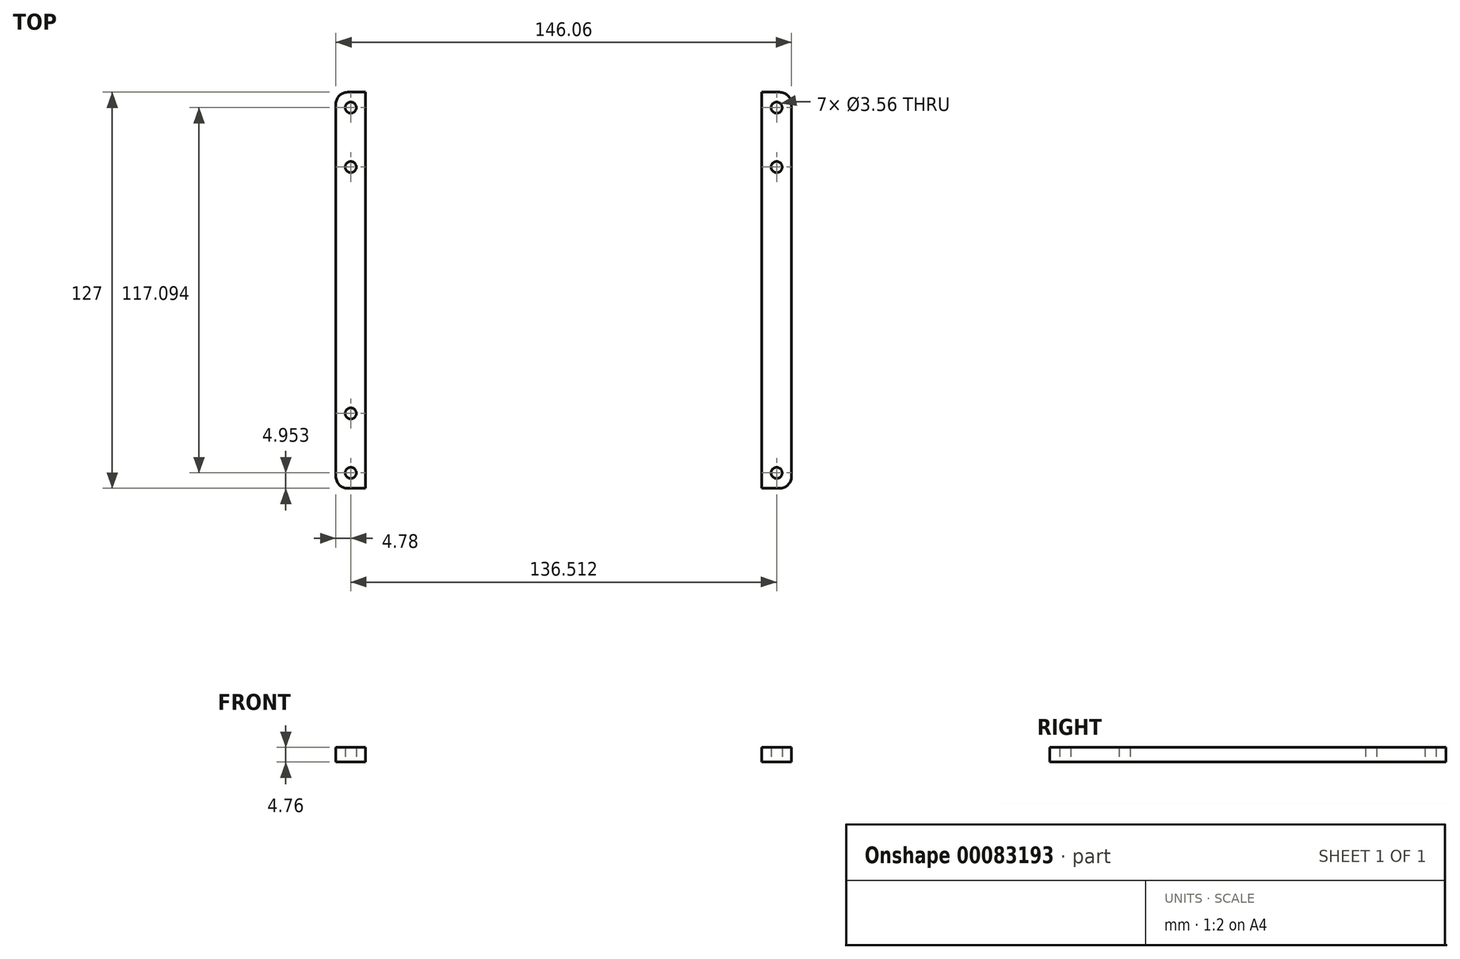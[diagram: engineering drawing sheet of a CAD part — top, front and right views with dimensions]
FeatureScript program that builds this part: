
annotation { "Feature Type Name" : "Feature", "Feature Type Description" : "" }
export const myFeature = defineFeature(function(context is Context, id is Id, definition is map)
    precondition{}
    {
        {
            var Q0;
            Q0=qCreatedBy(makeId("Top.planeOp"),FACE);
            var sketch = newSketch(context, id + "F0", { "sketchPlane" : qUnion([Q0])});
            skLineSegment(sketch, "E0.bottom", {"start": v(-73.03, 63.5) * mm, "end": v(73.03, 63.5) * mm});
            skLineSegment(sketch, "E0.top", {"start": v(-73.03, -63.5) * mm, "end": v(73.03, -63.5) * mm});
            skLineSegment(sketch, "E0.left", {"start": v(-73.03, 63.5) * mm, "end": v(-73.03, -63.5) * mm});
            skLineSegment(sketch, "E0.right", {"start": v(73.03, 63.5) * mm, "end": v(73.03, -63.5) * mm});
            skPoint(sketch, "E0.middle", {"position": v(0, 0) * mm});
            skLineSegment(sketch, "E1.bottom", {"start": v(-63.5, 63.5) * mm, "end": v(63.5, 63.5) * mm});
            skLineSegment(sketch, "E1.top", {"start": v(-63.5, -63.5) * mm, "end": v(63.5, -63.5) * mm});
            skLineSegment(sketch, "E1.left", {"start": v(-63.5, 63.5) * mm, "end": v(-63.5, -63.5) * mm});
            skLineSegment(sketch, "E1.right", {"start": v(63.5, 63.5) * mm, "end": v(63.5, -63.5) * mm});
            skLineSegment(sketch, "E2.bottom", {"start": v(-58.55, 58.55) * mm, "end": v(58.55, 58.55) * mm, "construction": true});
            skLineSegment(sketch, "E2.top", {"start": v(-58.55, -58.55) * mm, "end": v(58.55, -58.55) * mm, "construction": true});
            skLineSegment(sketch, "E2.left", {"start": v(-58.55, 58.55) * mm, "end": v(-58.55, -58.55) * mm, "construction": true});
            skLineSegment(sketch, "E2.right", {"start": v(58.55, 58.55) * mm, "end": v(58.55, -58.55) * mm, "construction": true});
            skLineSegment(sketch, "E3", {"start": v(-68.25, 58.55) * mm, "end": v(-68.25, -58.55) * mm, "construction": true});
            skLineSegment(sketch, "E4", {"start": v(68.26, -58.55) * mm, "end": v(68.26, 58.55) * mm, "construction": true});
            skPoint(sketch, "E5", {"position": v(-68.25, 39.5) * mm});
            skPoint(sketch, "E6", {"position": v(68.26, 39.5) * mm});
            skPoint(sketch, "E7", {"position": v(-68.25, -39.5) * mm});
            skPoint(sketch, "E8", {"position": v(68.26, -39.5) * mm});
            skSolve(sketch);
        }
        {
            var Q0;
            Q0=makeQuery(id+"F0.imprint","IMPRINT",FACE,{"disambiguationData":[TD([[makeQuery(id+"F0.imprint","IMPRINT",EDGE,{"derivedFrom":sQuery(id+"F0.wireOp",EDGE,"E1.bottom")}),-1.0]])]});
            var Q1;
            {var subQ0=sQuery(id+"F0.wireOp",EDGE,"E0.left");Q1=makeQuery(id+"F0.imprint","IMPRINT",FACE,{"disambiguationData":[TD([[makeQuery(id+"F0.imprint","IMPRINT",EDGE,{"derivedFrom":subQ0}),1.0]])]});}
            var Q2;
            {var subQ0=sQuery(id+"F0.wireOp",EDGE,"E0.right");Q2=makeQuery(id+"F0.imprint","IMPRINT",FACE,{"disambiguationData":[TD([[makeQuery(id+"F0.imprint","IMPRINT",EDGE,{"derivedFrom":subQ0}),-1.0]])]});}
            extrude(context, id + "F1", {"entities" : qUnion([Q0, Q1, Q2]), "depth" : 4.76 * mm});
        }
        {
            var Q0;
            Q0=sQuery(id+"F0.wireOp",VERTEX,"E3.start");
            var Q1;
            Q1=sQuery(id+"F0.wireOp",VERTEX,"E2.bottom.start");
            var Q2;
            Q2=sQuery(id+"F0.wireOp",VERTEX,"E5");
            var Q3;
            Q3=sQuery(id+"F0.wireOp",VERTEX,"E7");
            var Q4;
            Q4=sQuery(id+"F0.wireOp",VERTEX,"E3.end");
            var Q5;
            Q5=sQuery(id+"F0.wireOp",VERTEX,"E2.top.start");
            var Q6;
            Q6=sQuery(id+"F0.wireOp",VERTEX,"E2.right.end");
            var Q7;
            Q7=sQuery(id+"F0.wireOp",VERTEX,"E4.start");
            var Q8;
            Q8=sQuery(id+"F0.wireOp",VERTEX,"E4.end");
            var Q9;
            Q9=sQuery(id+"F0.wireOp",VERTEX,"E6");
            var Q10;
            Q10=sQuery(id+"F0.wireOp",VERTEX,"E2.right.start");
            var Q11;
            Q11=makeQuery(id+"F1.opExtrude","SWEPT_BODY",BODY,{"disambiguationData":[OSD([sQuery(id+"F0.wireOp",EDGE,"E0.bottom"),sQuery(id+"F0.wireOp",EDGE,"E0.top"),sQuery(id+"F0.wireOp",EDGE,"E0.left"),sQuery(id+"F0.wireOp",EDGE,"E0.right"),sQuery(id+"F0.wireOp",EDGE,"E1.bottom"),sQuery(id+"F0.wireOp",EDGE,"E1.top")])]});
            hole(context, id + "F2", {"style" : HoleStyle.SIMPLE, "endStyle" : HoleEndStyle.THROUGH, "oppositeDirection" : true, "holeDiameter" : 3.56 * mm, "locations" : qUnion([Q0, Q1, Q2, Q3, Q4, Q5, Q6, Q7, Q8, Q9, Q10]), "scope" : qUnion([Q11]), "isTappedThrough" : true});
        }
        {
            var Q0;
            Q0=makeQuery(id+"F1.opExtrude","SWEPT_EDGE",EDGE,{"disambiguationData":[OSD([sQuery(id+"F0.wireOp",EDGE,"E0.bottom"),sQuery(id+"F0.wireOp",EDGE,"E0.left")])]});
            var Q1;
            Q1=makeQuery(id+"F1.opExtrude","SWEPT_EDGE",EDGE,{"disambiguationData":[OSD([sQuery(id+"F0.wireOp",EDGE,"E0.top"),sQuery(id+"F0.wireOp",EDGE,"E0.left")])]});
            var Q2;
            Q2=makeQuery(id+"F1.opExtrude","SWEPT_EDGE",EDGE,{"disambiguationData":[OSD([sQuery(id+"F0.wireOp",EDGE,"E0.top"),sQuery(id+"F0.wireOp",EDGE,"E0.right")])]});
            var Q3;
            Q3=makeQuery(id+"F1.opExtrude","SWEPT_EDGE",EDGE,{"disambiguationData":[OSD([sQuery(id+"F0.wireOp",EDGE,"E0.bottom"),sQuery(id+"F0.wireOp",EDGE,"E0.right")])]});
            fillet(context, id + "F3", {"entities" : qUnion([Q0, Q1, Q2, Q3]), "radius" : 3.8 * mm, "tangentPropagation" : true, "allowEdgeOverflow" : false});
        }
    });
